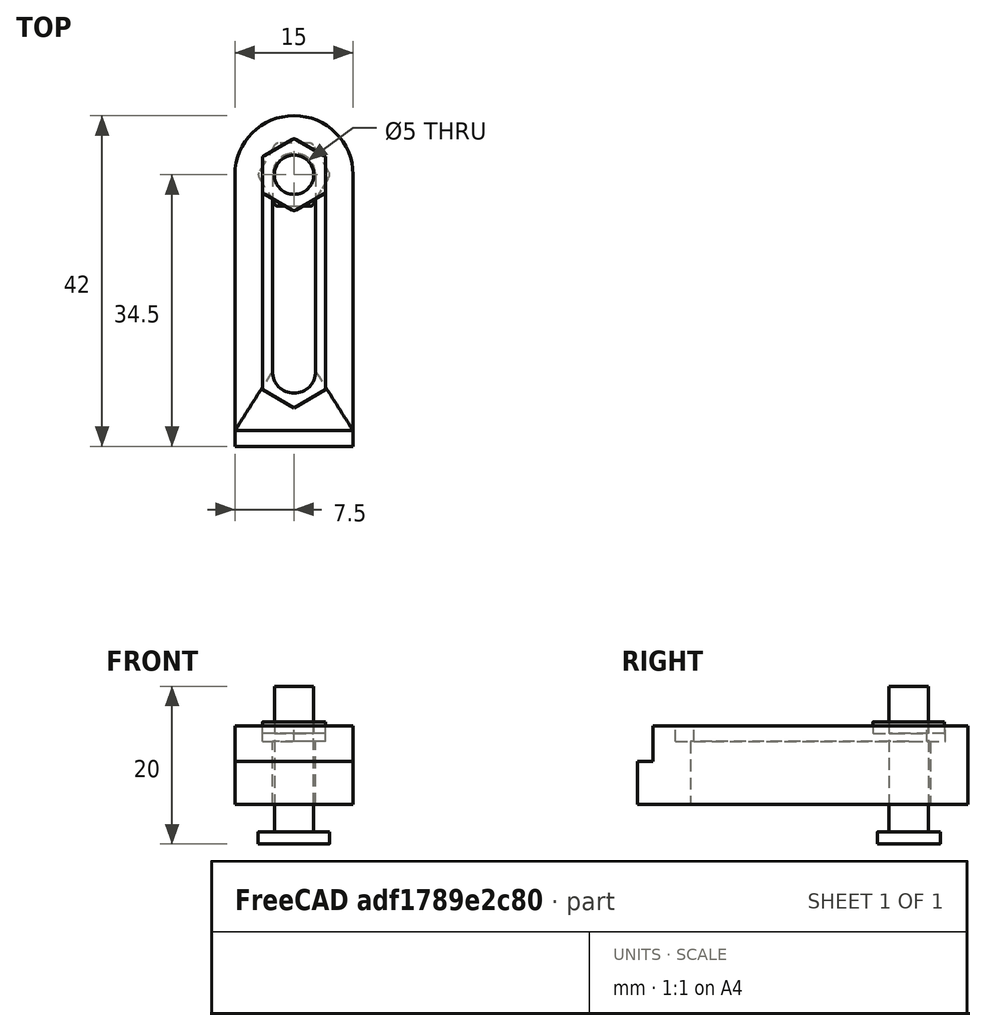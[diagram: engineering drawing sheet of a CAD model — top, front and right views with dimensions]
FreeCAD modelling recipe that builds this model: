
FCSTD DOCUMENT  (FreeCAD 0.14R3702 (Git))
Label: bride_rehaussable
License: CC-BY 3.0
LicenseURL: http://creativecommons.org/licenses/by/3.0/
objects: Part::Feature×19, Part::Extrusion×9, App::DocumentObjectGroup×5, Part::RuledSurface×4, Part::Part2DObjectPython×4, Part::MultiFuse×3, Part::Cut×2, Part::Box×1
note: 42 computed .brp shape members not serialized (recipe doc carries the construction recipe); baked Part::Feature solids carry a one-line shape summary decoded from their .brp

FEATURE [Part::Feature] Line
  shape: bbox 25 x 2e-07 x 2e-07 mm, 0 faces, 0 solids (baked)
FEATURE [Part::Feature] Line001
  shape: bbox 2e-07 x 25 x 2e-07 mm, 0 faces, 0 solids (baked)
FEATURE [Part::Feature] Line002
  shape: bbox 25 x 2e-07 x 2e-07 mm, 0 faces, 0 solids (baked)
FEATURE [Part::Feature] Line003
  shape: bbox 2e-07 x 25 x 2e-07 mm, 0 faces, 0 solids (baked)
FEATURE [App::DocumentObjectGroup] _  label="0"
  Group = -> [Line,Line001,Line002,Line003]
FEATURE [Part::Feature] Line004
  shape: bbox 15 x 2e-07 x 2e-07 mm, 0 faces, 0 solids (baked)
FEATURE [Part::Feature] Line005
  shape: bbox 2e-07 x 32.5 x 2e-07 mm, 0 faces, 0 solids (baked)
FEATURE [Part::Feature] Line006
  shape: bbox 2e-07 x 32.5 x 2e-07 mm, 0 faces, 0 solids (baked)
FEATURE [Part::Feature] Line007
  shape: bbox 2e-07 x 25 x 2e-07 mm, 0 faces, 0 solids (baked)
FEATURE [Part::Feature] Line008
  shape: bbox 2e-07 x 25 x 2e-07 mm, 0 faces, 0 solids (baked)
FEATURE [Part::Feature] Arc
  shape: bbox 15 x 7.5 x 2e-07 mm, 0 faces, 0 solids (baked)
FEATURE [App::DocumentObjectGroup] exterieur
  Group = -> [Line004,Line005,Line006,Arc]
FEATURE [Part::Feature] Arc001
  shape: bbox 5.5 x 2.75 x 2e-07 mm, 0 faces, 0 solids (baked)
FEATURE [Part::Feature] Arc002
  shape: bbox 5.5 x 2.75 x 2e-07 mm, 0 faces, 0 solids (baked)
FEATURE [App::DocumentObjectGroup] interieur
  Group = -> [Line007,Line008,Arc001,Arc002]
FEATURE [Part::RuledSurface] Ruled_Surface
  Curve1 = -> Arc001 [Edge1]
  Curve2 = -> Arc [Edge1]
  Orientation = 0
FEATURE [Part::RuledSurface] Ruled_Surface001
  Curve1 = -> Line008 [Edge1]
  Curve2 = -> Line006 [Edge1]
  Orientation = 0
FEATURE [Part::RuledSurface] Ruled_Surface002
  Curve1 = -> Arc002 [Edge1]
  Curve2 = -> Line004 [Edge1]
  Orientation = 0
FEATURE [Part::RuledSurface] Ruled_Surface003
  Curve1 = -> Line007 [Edge1]
  Curve2 = -> Line005 [Edge1]
  Orientation = 0
FEATURE [Part::Extrusion] Extrude
  Base = -> Ruled_Surface
  Dir = (0,0,10)
  Solid = false
FEATURE [Part::Extrusion] Extrude001
  Base = -> Ruled_Surface001
  Dir = (0,0,10)
  Solid = false
FEATURE [Part::Extrusion] Extrude002
  Base = -> Ruled_Surface002
  Dir = (0,0,10)
  Solid = false
FEATURE [Part::Extrusion] Extrude003
  Base = -> Ruled_Surface003
  Dir = (0,0,10)
  Solid = false
FEATURE [Part::MultiFuse] Fusion  label="Corp_brut"
  Shapes = -> [Extrude,Extrude001,Extrude002,Extrude003]
FEATURE [Part::Part2DObjectPython] Polygon  # Draft 2D object (typed FeaturePython)
  ChamferSize = 0
  DrawMode = 1
  FacesNumber = 6
  FilletRadius = 0.5
  Radius = 4
FEATURE [Part::Part2DObjectPython] Circle  # Draft 2D object (typed FeaturePython)
  FirstAngle = 0
  LastAngle = 0
  Placement = pos=(0,0,0) rot=(1,0,0;3.14159rad)
  Radius = 2.5
  Support = -> Polygon
FEATURE [Part::Part2DObjectPython] Polygon001  # Draft 2D object (typed FeaturePython)
  ChamferSize = 0
  DrawMode = 1
  FacesNumber = 6
  FilletRadius = 0.5
  Placement = pos=(10,0,0) rot=(0,0,1;0rad)
  Radius = 4
FEATURE [Part::Part2DObjectPython] Circle001  # Draft 2D object (typed FeaturePython)
  FirstAngle = 0
  LastAngle = 0
  Placement = pos=(10,0,0) rot=(1,0,0;3.14159rad)
  Radius = 2.5
  Support = -> Polygon001
FEATURE [Part::Extrusion] Extrude007
  Base = -> Circle
  Dir = (0,0,20)
  Solid = true
FEATURE [Part::Extrusion] Extrude008
  Base = -> Polygon
  Dir = (0,0,1.5)
  Solid = false
FEATURE [Part::Extrusion] Extrude009
  Base = -> Circle001
  Dir = (0,0,1.5)
  Solid = false
FEATURE [Part::Extrusion] Extrude010
  Base = -> Polygon001
  Dir = (0,0,1.5)
  Solid = false
FEATURE [Part::Cut] Cut001  label="ecrou"
  Base = -> Extrude010
  Placement = pos=(25,40,9) rot=(0,0,1;1.5708rad)
  Tool = -> Extrude009
FEATURE [Part::MultiFuse] Fusion004  label="vis"
  Placement = pos=(25,50,-5) rot=(0,0,1;0rad)
  Shapes = -> [Extrude007,Extrude008]
FEATURE [Part::Feature] Line030
  shape: bbox 4 x 2.309 x 2e-07 mm, 0 faces, 0 solids (baked)
FEATURE [Part::Feature] Line031
  shape: bbox 2e-07 x 29.62 x 2e-07 mm, 0 faces, 0 solids (baked)
FEATURE [Part::Feature] Line032
  shape: bbox 4 x 2.309 x 2e-07 mm, 0 faces, 0 solids (baked)
FEATURE [Part::Feature] Line033
  shape: bbox 4 x 2.309 x 2e-07 mm, 0 faces, 0 solids (baked)
FEATURE [Part::Feature] Line034
  shape: bbox 2e-07 x 29.62 x 2e-07 mm, 0 faces, 0 solids (baked)
FEATURE [Part::Feature] Line035
  shape: bbox 4 x 2.309 x 2e-07 mm, 0 faces, 0 solids (baked)
FEATURE [App::DocumentObjectGroup] exterieur2
  Group = -> [Line030,Line031,Line032,Line033,Line034,Line035]
FEATURE [App::DocumentObjectGroup] pince_fr
  Group = -> [_,exterieur,interieur,exterieur2]
FEATURE [Part::Feature] Face
  shape: bbox 8 x 34.24 x 2e-07 mm, 1 faces, 0 solids (baked)
FEATURE [Part::Extrusion] Extrude011  label="passe-ecrou"
  Base = -> Face
  Dir = (0,0,2)
  Placement = pos=(0,0,8) rot=(0,0,1;0rad)
  Solid = true
FEATURE [Part::Cut] Cut  label="bride-gen"
  Base = -> Fusion
  Tool = -> Extrude011
FEATURE [Part::Box] Box001  label="cale"
  Height = 5.5
  Length = 15
  Placement = pos=(17.5,15.5,0) rot=(0,0,1;0rad)
  Width = 2
FEATURE [Part::MultiFuse] Fusion005  label="Bride"
  Shapes = -> [Cut,Box001]
